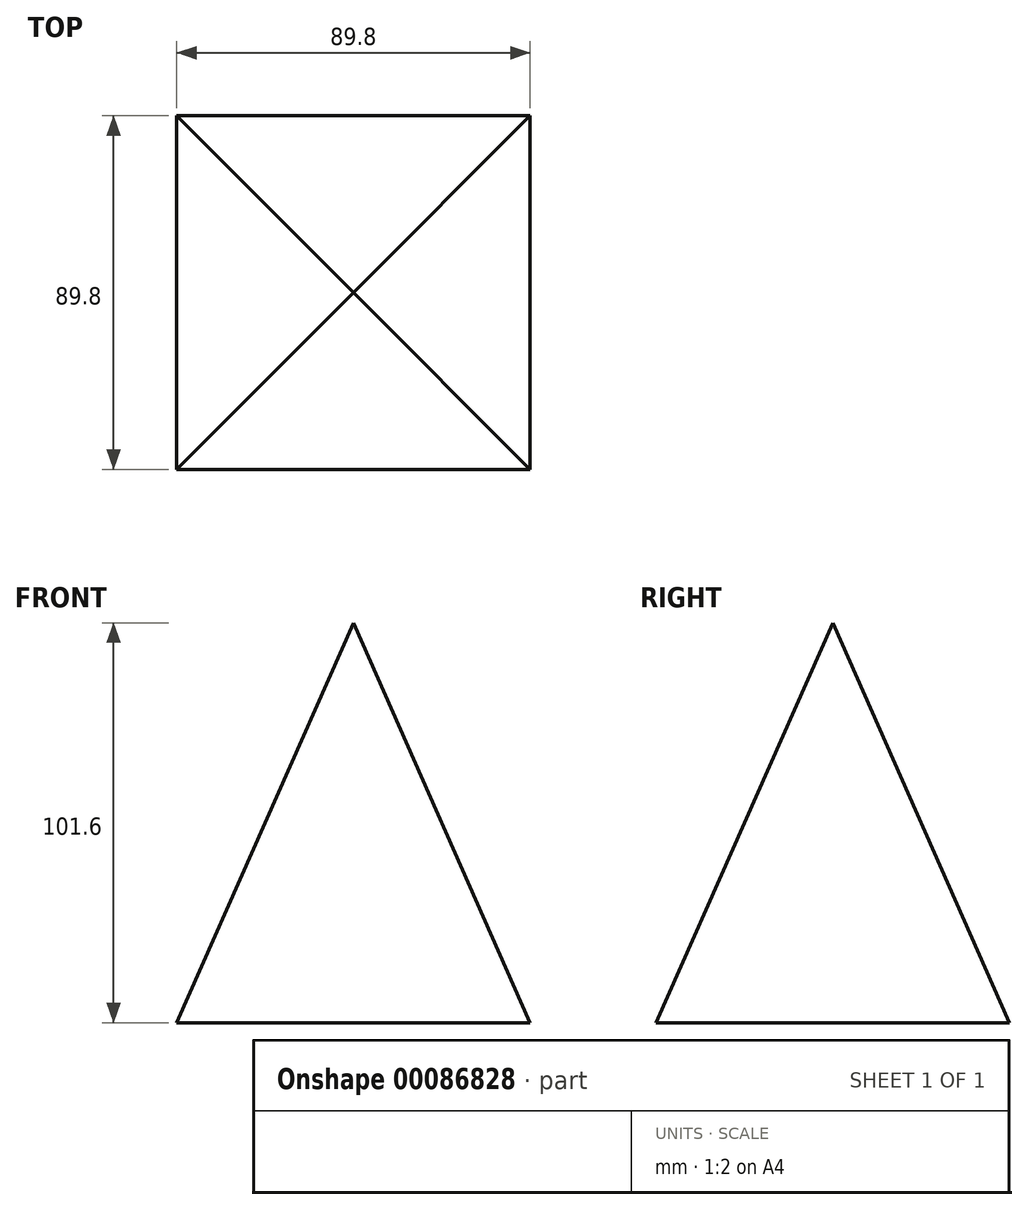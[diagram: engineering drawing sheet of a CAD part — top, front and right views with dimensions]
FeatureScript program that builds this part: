
annotation { "Feature Type Name" : "Feature", "Feature Type Description" : "" }
export const myFeature = defineFeature(function(context is Context, id is Id, definition is map)
    precondition{}
    {
        {
            var Q0;
            Q0=qCreatedBy(makeId("Front.planeOp"),FACE);
            var sketch = newSketch(context, id + "F0", { "sketchPlane" : qUnion([Q0])});
            skPoint(sketch, "E0", {"position": v(0, 101.6) * mm});
            skSolve(sketch);
        }
        {
            var Q0;
            Q0=qCreatedBy(makeId("Top.planeOp"),FACE);
            var sketch = newSketch(context, id + "F1", { "sketchPlane" : qUnion([Q0])});
            skCircle(sketch, "E1.cCircle", {"center": v(0, 0) * mm, "radius": 63.5 * mm, "construction": true});
            skLineSegment(sketch, "E1.0", {"start": v(44.9, 44.9) * mm, "end": v(44.9, -44.9) * mm});
            skLineSegment(sketch, "E1.1", {"start": v(44.9, -44.9) * mm, "end": v(-44.9, -44.9) * mm});
            skLineSegment(sketch, "E1.2", {"start": v(-44.9, -44.9) * mm, "end": v(-44.9, 44.9) * mm});
            skLineSegment(sketch, "E1.3", {"start": v(-44.9, 44.9) * mm, "end": v(44.9, 44.9) * mm});
            skSolve(sketch);
        }
        {
            var Q0;
            Q0=makeQuery(id+"F1.imprint","IMPRINT",FACE,{"disambiguationData":[TD([[makeQuery(id+"F1.imprint","IMPRINT",EDGE,{"derivedFrom":sQuery(id+"F1.wireOp",EDGE,"E1.0")}),-1.0]])]});
            var Q1;
            Q1=sQuery(id+"F0.wireOp",VERTEX,"E0");
            loft(context, id + "F2", {"sheetProfilesArray" : [{ "sheetProfileEntities" : qUnion([Q0]) }, { "sheetProfileEntities" : qUnion([Q1]) }]});
        }
    });
